# Revit family: Museum_Bench_BIM
name_source: partatom
category: Arredi
units: mm (PartAtom-declared; Revit-internal decimal feet)

## family parameters
Attiva taglio nelle viste = No
Basato su piano di lavoro = No
Condiviso = No
Numero OmniClass = 23.40.20.00
Origine composizione di rendering = Geometria famiglia
Punto di calcolo locali = No
Sempre verticale = Sì
Taglio con vuoti quando caricato = No
Titolo OmniClass = General Furniture and Specialties

## types (2) — shared parameters
AVAILABLE FINISHES = Ebonized black lacquer on Ash (EB) or bleached, white pigment, matte acrylic on Ash (BL). Raw effect lacquer on Oak (RE). Hand rubbed natural oil on Oak or Walnut (NA), or hand rubbed black oil on Walnut (BO). Inner frame: Satin nickel (SN), satin brass (SB), bronze (BZ) or gunmetal (GM) nanoceramic coated steel.
BASE MATERIAL = BASSAM_FELLOWS_WALNUT_BLACK_OIL_W-BO
BIM BADGE = https://bim.archiproducts.com
COLLECTION = Museum Bench
DEPTH = 420 mm  [stored 1.37795 ft]
Descrizione = Solid wood and brass bench
HEIGHT = 385 mm  [stored 1.26312 ft]
MATERIAL DESCRIPTION = Carved, solid wood exterior frame. Steel inner frame. Upholstery: Foam with edge banding. Single topstitch detail.
PRODUCT SHEET = https://www.archiproducts.com
Produttore = BassamFellows
STRUCTURE MATERIAL = BASSAM_FELLOWS_WALNUT_BLACK_OIL_W-BO
TECHNICAL SHEET = https://bassamfellows.com
UPHOLSTERY MATERIAL = BASSAM_FELLOWS_ELEGANT_LEATHER_48027_OLIVE
URL = https://bassamfellows.com
WIDTH = 1685 mm  [stored 5.52822 ft]
zero-valued in all types: Prospetto di default

## per-type parameters (varying)
| type | 2/3 CUSHION | CB-12 | FULL CUSHION | Modello |
| CB-31B | Sì | Sì | No | Museum Bench (2/3 Cushion and Removable Tray) |
| CB-31 | No | No | Sì | Museum Bench (Full Cushion) |

note: column(s) folded — value = type name in every type: PRODUCT CODE

note: [stored X ft] marks values corroborated as IEEE doubles in the binary element streams (Revit-internal decimal feet)

## geometry (parser evidence)
native form markers: Sweep x4
no freeform markers — native parametric forms only
